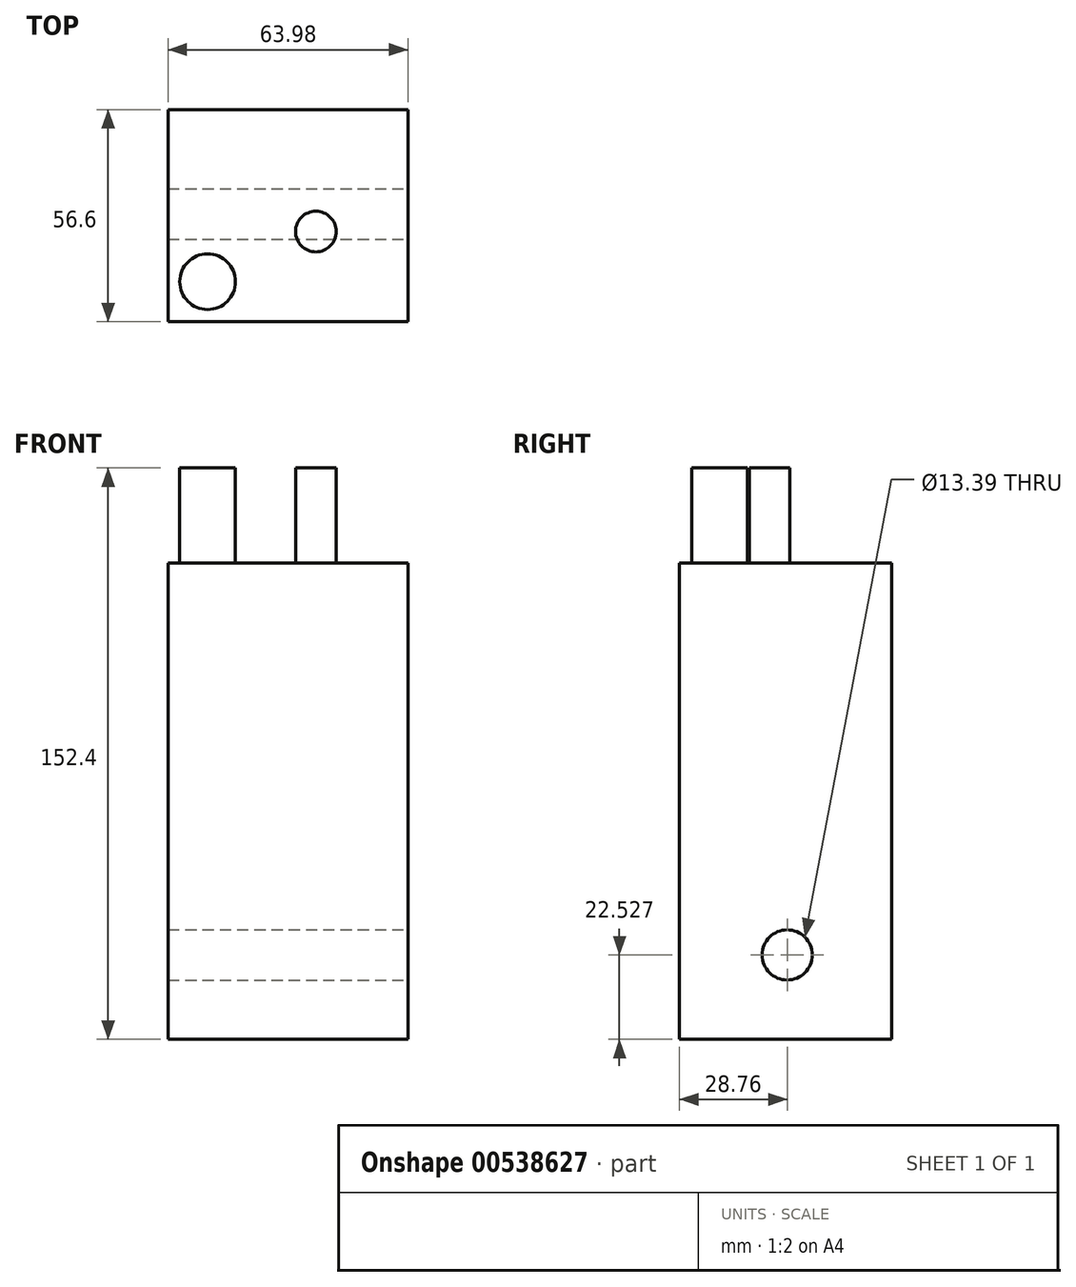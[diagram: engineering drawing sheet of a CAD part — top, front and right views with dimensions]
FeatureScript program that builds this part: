
annotation { "Feature Type Name" : "Feature", "Feature Type Description" : "" }
export const myFeature = defineFeature(function(context is Context, id is Id, definition is map)
    precondition{}
    {
        {
            var Q0;
            Q0=qCreatedBy(makeId("Top.planeOp"),FACE);
            var sketch = newSketch(context, id + "F0", { "sketchPlane" : qUnion([Q0])});
            skLineSegment(sketch, "E0.bottom", {"start": v(-35.4, 27.84) * mm, "end": v(28.58, 27.84) * mm});
            skLineSegment(sketch, "E0.top", {"start": v(-35.4, -28.76) * mm, "end": v(28.58, -28.76) * mm});
            skLineSegment(sketch, "E0.left", {"start": v(-35.4, 27.84) * mm, "end": v(-35.4, -28.76) * mm});
            skLineSegment(sketch, "E0.right", {"start": v(28.58, 27.84) * mm, "end": v(28.58, -28.76) * mm});
            skSolve(sketch);
        }
        {
            var Q0;
            Q0=makeQuery(id+"F0.imprint","IMPRINT",FACE,{"disambiguationData":[TD([[makeQuery(id+"F0.imprint","IMPRINT",EDGE,{"derivedFrom":sQuery(id+"F0.wireOp",EDGE,"E0.bottom")}),-1.0]])]});
            extrude(context, id + "F1", {"entities" : qUnion([Q0]), "depth" : 127 * mm, "offsetDistance" : 25.4 * mm});
        }
        {
            var Q0;
            Q0=makeQuery(id+"F1.opExtrude","CAP_FACE",FACE,{"disambiguationData":[OSD([sQuery(id+"F0.wireOp",EDGE,"E0.bottom"),sQuery(id+"F0.wireOp",EDGE,"E0.top"),sQuery(id+"F0.wireOp",EDGE,"E0.left"),sQuery(id+"F0.wireOp",EDGE,"E0.right")])],"isStart":false});
            var sketch = newSketch(context, id + "F2", { "sketchPlane" : qUnion([Q0])});
            skCircle(sketch, "E1", {"center": v(4.03, -4.7) * mm, "radius": 5.42 * mm});
            skSolve(sketch);
        }
        {
            var Q0;
            Q0 = qSketchRegion(id + "F2", true);
            extrude(context, id + "F3", {"entities" : qUnion([Q0]), "operationType" : NewBodyOperationType.ADD, "depth" : 25.4 * mm, "offsetDistance" : 25.4 * mm});
        }
        {
            var Q0;
            Q0=makeQuery(id+"F1.opExtrude","SWEPT_FACE",FACE,{"disambiguationData":[OSD([sQuery(id+"F0.wireOp",EDGE,"E0.right")])]});
            var sketch = newSketch(context, id + "F4", { "sketchPlane" : qUnion([Q0])});
            skCircle(sketch, "E2", {"center": v(0, 22.53) * mm, "radius": 6.7 * mm});
            skSolve(sketch);
        }
        {
            var Q0;
            Q0=makeQuery(id+"F4.imprint","IMPRINT",FACE,{"disambiguationData":[TD([[makeQuery(id+"F4.imprint","IMPRINT",EDGE,{"derivedFrom":sQuery(id+"F4.wireOp",EDGE,"E2")}),1.0]])]});
            extrude(context, id + "F5", {"entities" : qUnion([Q0]), "operationType" : NewBodyOperationType.REMOVE, "oppositeDirection" : true, "depth" : 85.1 * mm, "offsetDistance" : 25.4 * mm});
        }
        {
            var Q0;
            Q0=makeQuery(id+"F1.opExtrude","CAP_FACE",FACE,{"disambiguationData":[OSD([sQuery(id+"F0.wireOp",EDGE,"E0.bottom"),sQuery(id+"F0.wireOp",EDGE,"E0.top"),sQuery(id+"F0.wireOp",EDGE,"E0.left"),sQuery(id+"F0.wireOp",EDGE,"E0.right")])],"isStart":false});
            var sketch = newSketch(context, id + "F6", { "sketchPlane" : qUnion([Q0])});
            skCircle(sketch, "E3", {"center": v(-24.85, -18.08) * mm, "radius": 7.43 * mm});
            skSolve(sketch);
        }
        {
            var Q0;
            Q0 = qSketchRegion(id + "F6", true);
            extrude(context, id + "F7", {"entities" : qUnion([Q0]), "operationType" : NewBodyOperationType.ADD, "depth" : 25.4 * mm, "offsetDistance" : 25.4 * mm});
        }
    });
